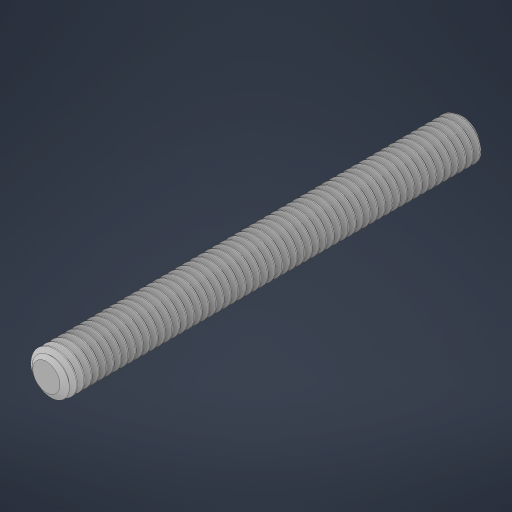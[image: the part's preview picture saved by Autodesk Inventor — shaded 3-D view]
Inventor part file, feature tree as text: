
AUTODESK INVENTOR PART (.ipt)
format: ipt  version: 2023 (Build 270158000, 158)  size: 1,581,568 bytes
history: native  units: in
note: dims shown in document units (in); Inventor stores cm internally (conversion verified against a paired STEP export)
features: mirror x1
ambient origin geometry x8: Origin, YZ Plane, XZ Plane, XY Plane, X Axis, Y Axis, Z Axis, Center Point
bodies: Solid1 (feature_tree)
feature tree (1):
  mirror  "Mirror1"
